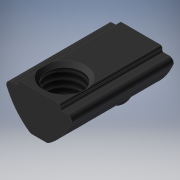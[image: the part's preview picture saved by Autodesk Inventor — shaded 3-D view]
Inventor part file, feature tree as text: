
AUTODESK INVENTOR PART (.ipt)
format: ipt  version: 2019 (Build 230136000, 136)  size: 205,824 bytes
history: native  units: mm
features: other x7, sketch x4, revolve x2, extrude x1, thread x1, hole x1
ambient origin geometry x8: Origin, YZ Plane, XZ Plane, XY Plane, X Axis, Y Axis, Z Axis, Center Point
bodies: Solid1 (feature_tree)
feature tree (16):
  extrude  "Extrusion1"  TaperAngle=360.0deg  [1 undecoded]
  revolve  "Revolution1"  Angle=360.0deg
  thread  "Thread1"  [1 undecoded]
  hole  "Hole1"  [1 undecoded]
  revolve  "Revolution2"  [1 undecoded]
  other  "nut_to_bolt_XY"
  other  "nut_to_bolt_YZ"
  other  "nut_to_bolt_ZX"
  other  "nut_to_bolt_X"
  other  "nut_to_bolt_Y"
  other  "nut_to_bolt_Z"
  other  "nut_to_bolt_Center"
  sketch  "Sketch_1"  dims[d0=12.0mm d1=0.0mm d2=360.0deg]
  sketch  "Sketch_2"  dims[d3=3.834mm d4=0.0mm]
  sketch  "Sketch3"  dims[d5=3.0mm d6=6.0mm d7=4.0mm d8=2.0mm d9=90.0deg d10=3.28mm d11=0.0mm d12=360.0deg]
  sketch  "Sketch_5"
note: 4 required parameter values undecoded (feature->parameter linkage not recoverable at this tier; creation-order binding heuristic only, values carry confidence <= 0.55)
